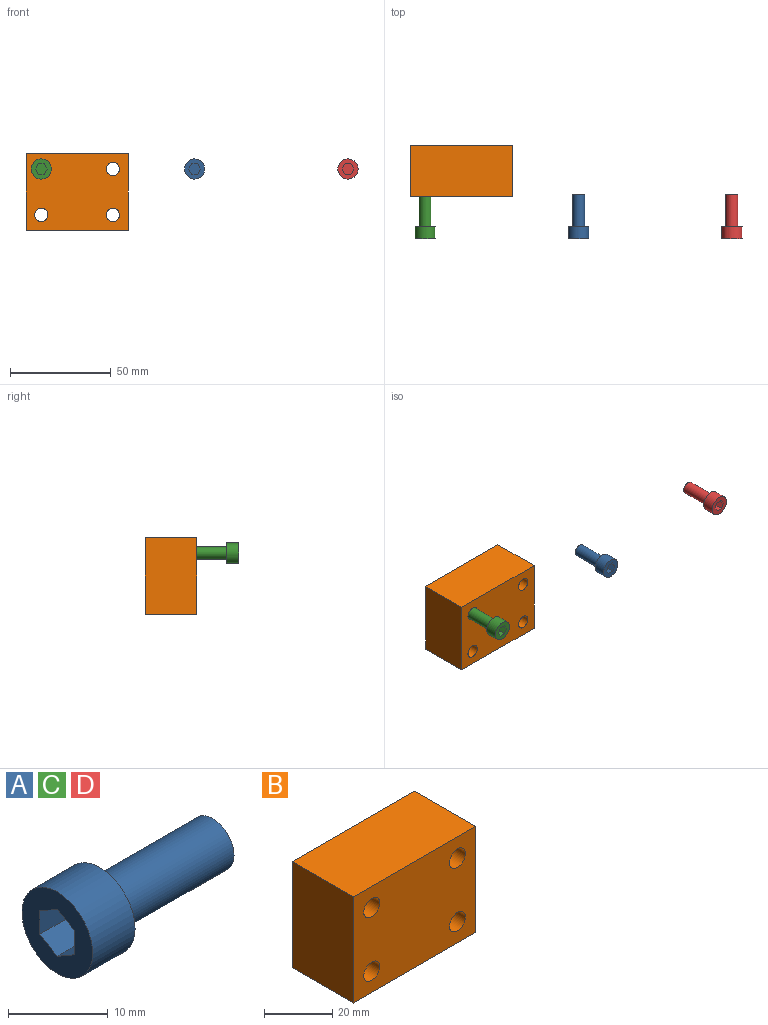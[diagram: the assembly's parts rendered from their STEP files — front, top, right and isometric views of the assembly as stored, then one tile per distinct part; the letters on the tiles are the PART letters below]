
ASSEMBLY  parts=4 mates=1
PART A: 12 faces, bbox 22x10x10 mm
  f0: plane 10x10mm, normal (-1,0,0), area 56.9mm2, adj f4,f5,f6,f7,f8,f9,f10
  f1: plane 6x6mm, normal (1,0,0), area 28.3mm2, adj f2
  f2: cylinder r=3mm len=16mm, axis (-1,0,0), area 301.6mm2, adj f1,f3
  f3: plane 10x10mm, normal (1,0,0), area 50.3mm2, adj f2,f4
  f4: cylinder r=5mm len=10mm, axis (-1,0,0), area 188.5mm2, adj f0,f3
  f5: plane 4.5x2.5mm, normal (0,0.5,-0.87), area 13mm2, adj f0,f6,f10,f11
  f6: plane 4.5x2.5mm, normal (0,-0.5,-0.87), area 13mm2, adj f0,f5,f7,f11
  f7: plane 4.5x2.89mm, normal (0,-1,0), area 13mm2, adj f0,f6,f8,f11
  f8: plane 4.5x2.5mm, normal (0,-0.5,0.87), area 13mm2, adj f0,f7,f9,f11
  f9: plane 4.5x2.5mm, normal (0,0.5,0.87), area 13mm2, adj f0,f8,f10,f11
  f10: plane 4.5x2.89mm, normal (0,1,0), area 13mm2, adj f0,f5,f9,f11
  f11: plane 5.77x5mm, normal (-1,0,0), area 21.7mm2, adj f5,f6,f7,f8,f9,f10
PART B: 10 faces, bbox 50.8x25.4x38.1 mm
  f0: plane 38.1x25.4mm, normal (-1,0,0), area 967.7mm2, adj f1,f3,f4,f5
  f1: plane 50.8x25.4mm, normal (0,0,-1), area 1290.3mm2, adj f0,f2,f4,f5
  f2: plane 38.1x25.4mm, normal (1,0,0), area 967.7mm2, adj f1,f3,f4,f5
  f3: plane 50.8x25.4mm, normal (0,0,1), area 1290.3mm2, adj f0,f2,f4,f5
  f4: plane 50.8x38.1mm, normal (0,-1,0), area 1798.6mm2, adj f0,f1,f2,f3,f6,f7,f8,f9
  f5: plane 50.8x38.1mm, normal (0,1,0), area 1798.6mm2, adj f0,f1,f2,f3,f6,f7,f8,f9
  f6: cylinder r=3.3mm len=25.4mm, axis (0,-1,0), area 526.7mm2, adj f4,f5
  f7: cylinder r=3.3mm len=25.4mm, axis (0,-1,0), area 526.7mm2, adj f4,f5
  f8: cylinder r=3.3mm len=25.4mm, axis (0,-1,0), area 526.7mm2, adj f4,f5
  f9: cylinder r=3.3mm len=25.4mm, axis (0,-1,0), area 526.7mm2, adj f4,f5
PART C: same geometry as A
PART D: same geometry as A
PLACE A rot(axis=(-0.58,-0.58,0.58),120deg) t=(41.5,-33.67,22.47)mm
PLACE B t=(-42.32,6.65,-8.01)mm
PLACE C rot(axis=(-0.58,-0.58,0.58),120deg) t=(-34.7,-33.67,22.47)mm
PLACE D rot(axis=(-0.58,-0.58,0.58),120deg) t=(117.7,-33.67,22.47)mm
MATE slider C.f2 <-> B.f6  axis (0,-1,0) through (-34.7,-25.67,22.47)mm
